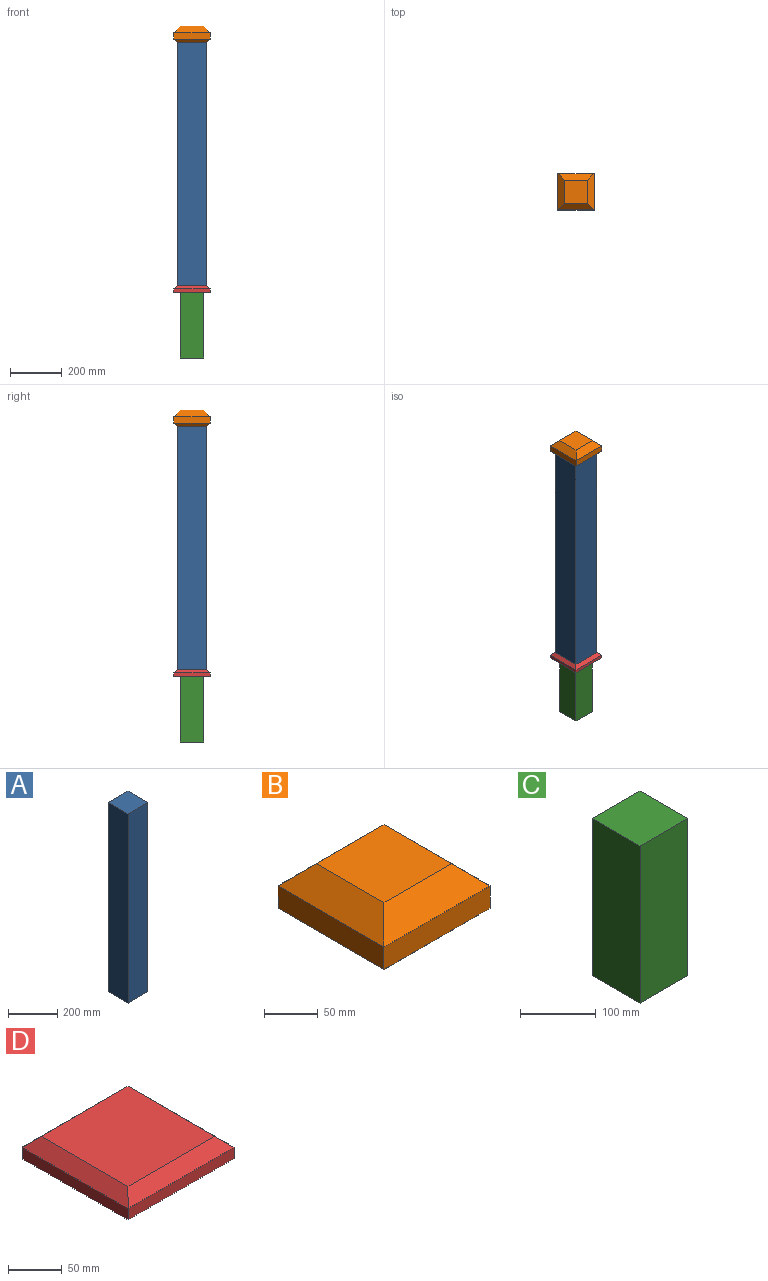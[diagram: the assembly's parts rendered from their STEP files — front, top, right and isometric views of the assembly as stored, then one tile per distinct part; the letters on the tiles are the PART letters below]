
ASSEMBLY  parts=4 mates=3
PART A: 6 faces, bbox 114.3x114.3x939.8 mm
  f0: plane 939.8x114.3mm, normal (-1,0,0), area 107419.1mm2, adj f1,f3,f4,f5
  f1: plane 939.8x114.3mm, normal (0,-1,0), area 107419.1mm2, adj f0,f2,f4,f5
  f2: plane 939.8x114.3mm, normal (1,0,0), area 107419.1mm2, adj f1,f3,f4,f5
  f3: plane 939.8x114.3mm, normal (0,1,0), area 107419.1mm2, adj f0,f2,f4,f5
  f4: plane 114.3x114.3mm, normal (0,0,1), area 13064.5mm2, adj f0,f1,f2,f3
  f5: plane 114.3x114.3mm, normal (0,0,-1), area 13064.5mm2, adj f0,f1,f2,f3
PART B: 14 faces, bbox 139.7x139.7x63.5 mm
  f0: plane 139.7x25.4mm, normal (1,0,0), area 3548.4mm2, adj f1,f3,f9,f13
  f1: plane 139.7x25.4mm, normal (0,1,0), area 3548.4mm2, adj f0,f2,f7,f11
  f2: plane 139.7x25.4mm, normal (-1,0,0), area 3548.4mm2, adj f1,f3,f6,f10
  f3: plane 139.7x25.4mm, normal (0,-1,0), area 3548.4mm2, adj f0,f2,f8,f12
  f4: plane 88.9x88.9mm, normal (0,0,1), area 7903.2mm2, adj f10,f11,f12,f13
  f5: plane 114.3x114.3mm, normal (0,0,-1), area 13064.5mm2, adj f6,f7,f8,f9
  f6: plane 139.7x12.7mm, normal (-0.71,0,-0.71), area 2281mm2, adj f2,f5,f7,f8
  f7: plane 139.7x12.7mm, normal (0,0.71,-0.71), area 2281mm2, adj f1,f5,f6,f9
  f8: plane 139.7x12.7mm, normal (0,-0.71,-0.71), area 2281mm2, adj f3,f5,f6,f9
  f9: plane 139.7x12.7mm, normal (0.71,0,-0.71), area 2281mm2, adj f0,f5,f7,f8
  f10: plane 139.7x25.4mm, normal (-0.71,0,0.71), area 4105.8mm2, adj f2,f4,f11,f12
  f11: plane 139.7x25.4mm, normal (0,0.71,0.71), area 4105.8mm2, adj f1,f4,f10,f13
  f12: plane 139.7x25.4mm, normal (0,-0.71,0.71), area 4105.8mm2, adj f3,f4,f10,f13
  f13: plane 139.7x25.4mm, normal (0.71,0,0.71), area 4105.8mm2, adj f0,f4,f11,f12
PART C: 6 faces, bbox 88.9x88.9x254 mm
  f0: plane 254x88.9mm, normal (0,-1,0), area 22580.6mm2, adj f1,f3,f4,f5
  f1: plane 254x88.9mm, normal (1,0,0), area 22580.6mm2, adj f0,f2,f4,f5
  f2: plane 254x88.9mm, normal (0,1,0), area 22580.6mm2, adj f1,f3,f4,f5
  f3: plane 254x88.9mm, normal (-1,0,0), area 22580.6mm2, adj f0,f2,f4,f5
  f4: plane 88.9x88.9mm, normal (0,0,1), area 7903.2mm2, adj f0,f1,f2,f3
  f5: plane 88.9x88.9mm, normal (0,0,-1), area 7903.2mm2, adj f0,f1,f2,f3
PART D: 10 faces, bbox 139.7x139.7x25.4 mm
  f0: plane 139.7x12.7mm, normal (0,1,0), area 1774.2mm2, adj f1,f3,f5,f7
  f1: plane 139.7x12.7mm, normal (-1,0,0), area 1774.2mm2, adj f0,f2,f5,f6
  f2: plane 139.7x12.7mm, normal (0,-1,0), area 1774.2mm2, adj f1,f3,f5,f8
  f3: plane 139.7x12.7mm, normal (1,0,0), area 1774.2mm2, adj f0,f2,f5,f9
  f4: plane 114.3x114.3mm, normal (0,0,1), area 13064.5mm2, adj f6,f7,f8,f9
  f5: plane 139.7x139.7mm, normal (0,0,-1), area 19516.1mm2, adj f0,f1,f2,f3
  f6: plane 139.7x12.7mm, normal (-0.71,0,0.71), area 2281mm2, adj f1,f4,f7,f8
  f7: plane 139.7x12.7mm, normal (0,0.71,0.71), area 2281mm2, adj f0,f4,f6,f9
  f8: plane 139.7x12.7mm, normal (0,-0.71,0.71), area 2281mm2, adj f2,f4,f6,f9
  f9: plane 139.7x12.7mm, normal (0.71,0,0.71), area 2281mm2, adj f3,f4,f7,f8
PLACE A t=(-175.11,-127,-990.6)mm
PLACE B t=(0,0,-50.8)mm
PLACE C t=(-24.16,-144.26,-1270)mm
PLACE D t=(-187.81,28.5,-1016)mm
MATE fastened A.f4 <-> B.f5  axis (0,0,1) through (-117.96,-69.85,-50.8)mm
MATE fastened C.f4 <-> D.f5  axis (0,0,1) through (-117.96,-69.85,-1016)mm
MATE fastened D.f4 <-> A.f5  axis (0,0,1) through (-117.96,-69.85,-990.6)mm
